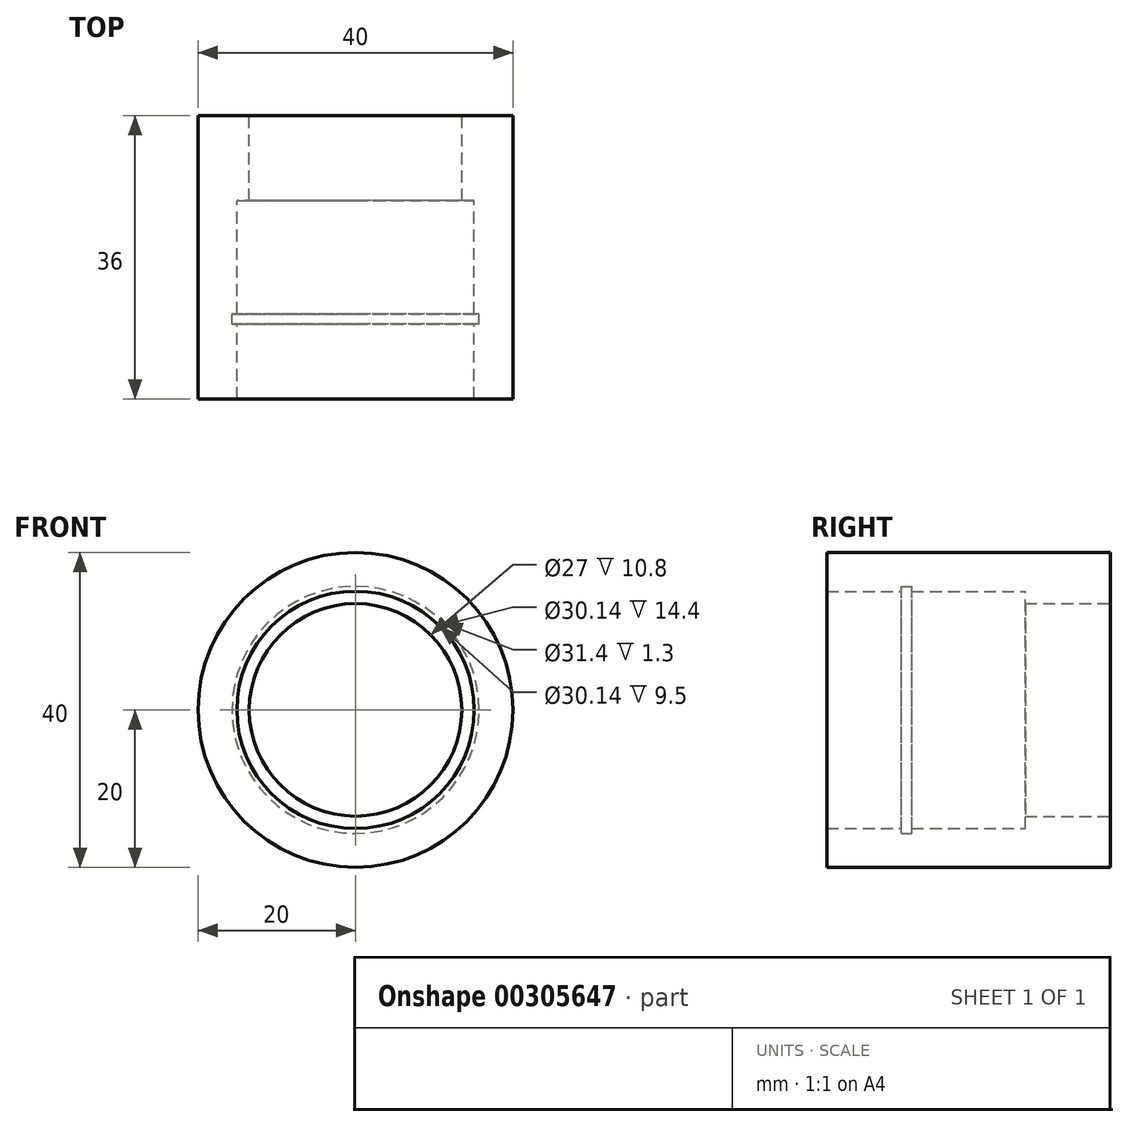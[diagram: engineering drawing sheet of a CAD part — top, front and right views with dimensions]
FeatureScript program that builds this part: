
annotation { "Feature Type Name" : "Feature", "Feature Type Description" : "" }
export const myFeature = defineFeature(function(context is Context, id is Id, definition is map)
    precondition{}
    {
        {
            var Q0;
            Q0=qCreatedBy(makeId("Front.planeOp"),FACE);
            var sketch = newSketch(context, id + "F0", { "sketchPlane" : qUnion([Q0])});
            skCircle(sketch, "E0", {"center": v(0, 0) * mm, "radius": 20 * mm});
            skCircle(sketch, "E1", {"center": v(0, 0) * mm, "radius": 15.07 * mm});
            skSolve(sketch);
        }
        {
            var Q0;
            Q0=makeQuery(id+"F0.imprint","IMPRINT",FACE,{"disambiguationData":[TD([[makeQuery(id+"F0.imprint","IMPRINT",EDGE,{"derivedFrom":sQuery(id+"F0.wireOp",EDGE,"E0")}),1.0]])]});
            var Q1;
            Q1=makeQuery(id+"F0.imprint","IMPRINT",FACE,{"disambiguationData":[TD([[makeQuery(id+"F0.imprint","IMPRINT",EDGE,{"derivedFrom":sQuery(id+"F0.wireOp",EDGE,"E1")}),1.0]])]});
            extrude(context, id + "F1", {"entities" : qUnion([Q0, Q1]), "depth" : 10.8 * mm});
        }
        {
            var Q0;
            Q0=makeQuery(id+"F1.opExtrude","CAP_FACE",FACE,{"disambiguationData":[OSD([sQuery(id+"F0.wireOp",EDGE,"E0")])],"isStart":true});
            var sketch = newSketch(context, id + "F2", { "sketchPlane" : qUnion([Q0])});
            skCircle(sketch, "E2", {"center": v(0, 0) * mm, "radius": 13.5 * mm});
            skSolve(sketch);
        }
        {
            var Q0;
            Q0=qSketchRegion(id+"F2",true);
            extrude(context, id + "F3", {"entities" : qUnion([Q0]), "operationType" : NewBodyOperationType.REMOVE, "oppositeDirection" : true, "depth" : 10.8 * mm});
        }
        {
            var Q0;
            Q0=makeQuery(id+"F1.opExtrude","CAP_FACE",FACE,{"disambiguationData":[OSD([sQuery(id+"F0.wireOp",EDGE,"E0")])],"isStart":false});
            var sketch = newSketch(context, id + "F4", { "sketchPlane" : qUnion([Q0])});
            skCircle(sketch, "E3", {"center": v(0, 0) * mm, "radius": 15.07 * mm});
            skSolve(sketch);
        }
        {
            var Q0;
            Q0=makeQuery(id+"F4.imprint","IMPRINT",FACE,{"disambiguationData":[TD([[makeQuery(id+"F4.imprint","IMPRINT",EDGE,{"derivedFrom":sQuery(id+"F4.wireOp",EDGE,"E3")}),-1.0]])]});
            extrude(context, id + "F5", {"entities" : qUnion([Q0]), "operationType" : NewBodyOperationType.ADD, "depth" : 14.4 * mm});
        }
        {
            var Q0;
            Q0=makeQuery(id+"F5.opExtrude","CAP_FACE",FACE,{"disambiguationData":[OSD([sQuery(id+"F0.wireOp",EDGE,"E0"),sQuery(id+"F4.wireOp",EDGE,"E3")])],"isStart":false});
            var sketch = newSketch(context, id + "F6", { "sketchPlane" : qUnion([Q0])});
            skCircle(sketch, "E4", {"center": v(0, 0) * mm, "radius": 15.7 * mm});
            skSolve(sketch);
        }
        {
            var Q0;
            Q0=makeQuery(id+"F6.imprint","IMPRINT",FACE,{"disambiguationData":[TD([[makeQuery(id+"F6.imprint","IMPRINT",EDGE,{"derivedFrom":sQuery(id+"F6.wireOp",EDGE,"E4")}),-1.0]])]});
            extrude(context, id + "F7", {"entities" : qUnion([Q0]), "operationType" : NewBodyOperationType.ADD, "depth" : 1.3 * mm});
        }
        {
            var Q0;
            Q0=makeQuery(id+"F7.opExtrude","CAP_FACE",FACE,{"disambiguationData":[OSD([sQuery(id+"F0.wireOp",EDGE,"E0"),sQuery(id+"F6.wireOp",EDGE,"E4")])],"isStart":false});
            var sketch = newSketch(context, id + "F8", { "sketchPlane" : qUnion([Q0])});
            skCircle(sketch, "E5", {"center": v(0, 0) * mm, "radius": 15.07 * mm});
            skSolve(sketch);
        }
        {
            var Q0;
            Q0=makeQuery(id+"F8.imprint","IMPRINT",FACE,{"disambiguationData":[TD([[makeQuery(id+"F8.imprint","IMPRINT",EDGE,{"derivedFrom":sQuery(id+"F8.wireOp",EDGE,"E5")}),-1.0]])]});
            var Q1;
            Q1=makeQuery(id+"F8.imprint","IMPRINT",FACE,{"disambiguationData":[TD([[makeQuery(id+"F8.imprint","IMPRINT",EDGE,{"derivedFrom":makeQuery(id+"F7.opExtrude","CAP_EDGE",EDGE,{"disambiguationData":[OSD([sQuery(id+"F6.wireOp",EDGE,"E4")])],"isStart":false})}),-1.0]])]});
            extrude(context, id + "F9", {"entities" : qUnion([Q0, Q1]), "operationType" : NewBodyOperationType.ADD, "depth" : 9.5 * mm});
        }
    });
